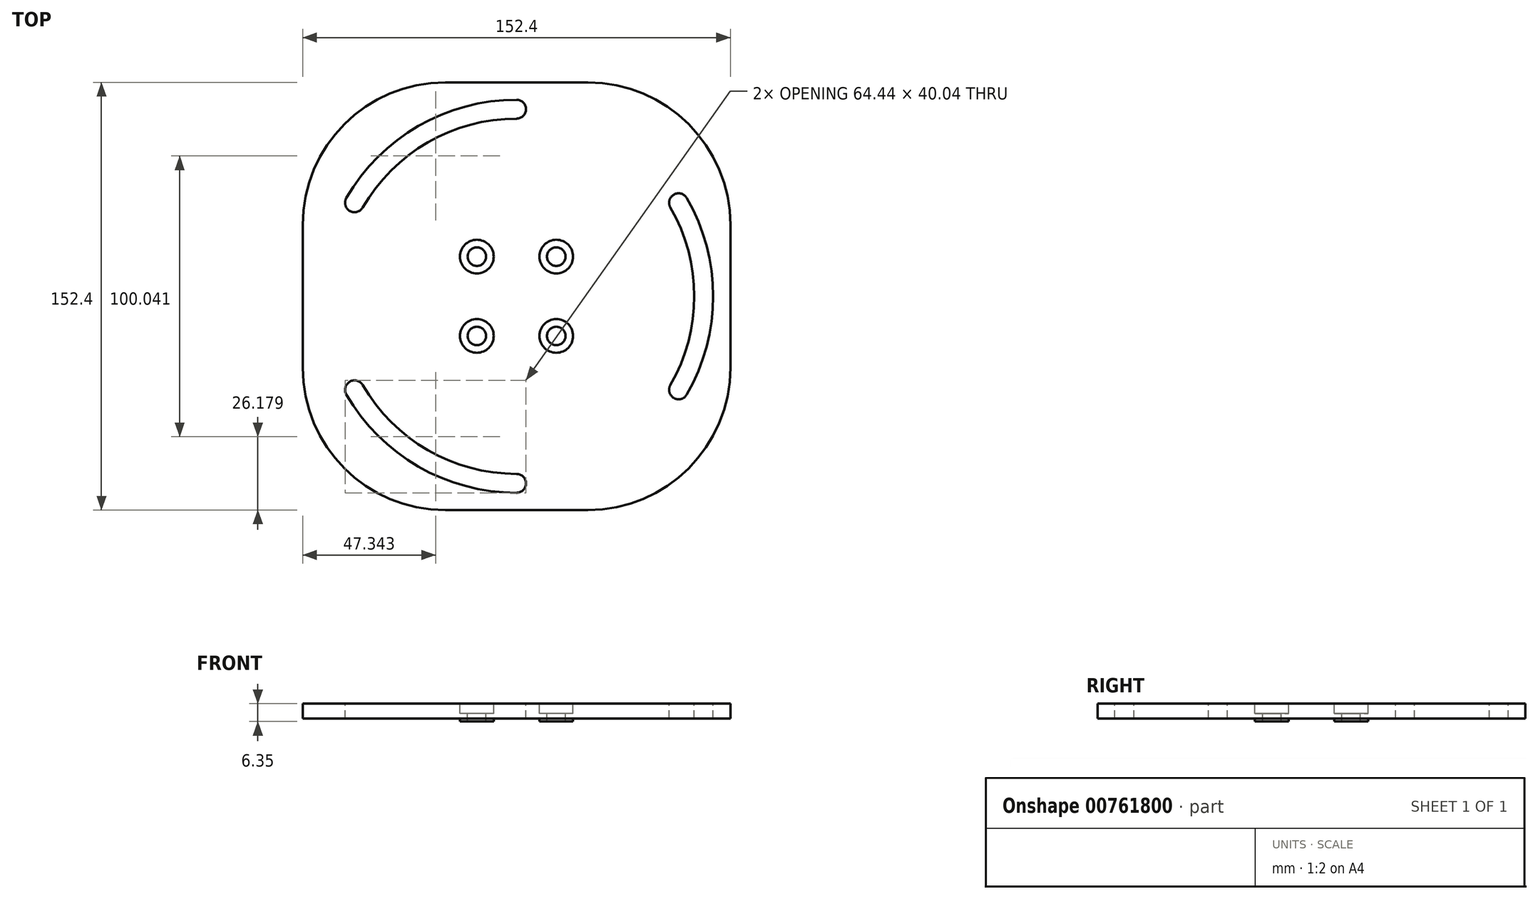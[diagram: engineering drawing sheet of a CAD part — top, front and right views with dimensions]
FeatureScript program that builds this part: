
annotation { "Feature Type Name" : "Feature", "Feature Type Description" : "" }
export const myFeature = defineFeature(function(context is Context, id is Id, definition is map)
    precondition{}
    {
        {
            var Q0;
            Q0=qCreatedBy(makeId("Top.planeOp"),FACE);
            var sketch = newSketch(context, id + "F0", { "sketchPlane" : qUnion([Q0])});
            skLineSegment(sketch, "E0.bottom", {"start": v(-76.2, 76.2) * mm, "end": v(76.2, 76.2) * mm});
            skLineSegment(sketch, "E0.top", {"start": v(-76.2, -76.2) * mm, "end": v(76.2, -76.2) * mm});
            skLineSegment(sketch, "E0.left", {"start": v(-76.2, 76.2) * mm, "end": v(-76.2, -76.2) * mm});
            skLineSegment(sketch, "E0.right", {"start": v(76.2, 76.2) * mm, "end": v(76.2, -76.2) * mm});
            skCircle(sketch, "E1", {"center": v(0, 0) * mm, "radius": 20 * mm, "construction": true});
            skLineSegment(sketch, "E2.bottom", {"start": v(-66.68, 66.68) * mm, "end": v(66.68, 66.68) * mm, "construction": true});
            skLineSegment(sketch, "E2.top", {"start": v(-66.68, -66.68) * mm, "end": v(66.67, -66.68) * mm, "construction": true});
            skLineSegment(sketch, "E2.left", {"start": v(-66.67, 66.68) * mm, "end": v(-66.68, -66.68) * mm, "construction": true});
            skLineSegment(sketch, "E2.right", {"start": v(66.68, 66.68) * mm, "end": v(66.67, -66.68) * mm, "construction": true});
            skLineSegment(sketch, "E3", {"start": v(0, 66.68) * mm, "end": v(0, -66.68) * mm, "construction": true});
            skLineSegment(sketch, "E4", {"start": v(-66.67, 0) * mm, "end": v(66.67, 0) * mm, "construction": true});
            skLineSegment(sketch, "E5.bottom", {"start": v(-14.14, 14.14) * mm, "end": v(14.14, 14.14) * mm});
            skLineSegment(sketch, "E5.top", {"start": v(-14.14, -14.14) * mm, "end": v(14.14, -14.14) * mm});
            skLineSegment(sketch, "E5.left", {"start": v(-14.14, 14.14) * mm, "end": v(-14.14, -14.14) * mm});
            skLineSegment(sketch, "E5.right", {"start": v(14.14, 14.14) * mm, "end": v(14.14, -14.14) * mm});
            skCircle(sketch, "E6", {"center": v(0, 0) * mm, "radius": 66.67 * mm, "construction": true});
            skLineSegment(sketch, "E7", {"start": v(0, 0) * mm, "end": v(-57.74, 33.34) * mm, "construction": true});
            skLineSegment(sketch, "E8", {"start": v(0, 0) * mm, "end": v(-57.74, -33.34) * mm, "construction": true});
            skLineSegment(sketch, "E9", {"start": v(0, 0) * mm, "end": v(57.74, -33.34) * mm, "construction": true});
            skLineSegment(sketch, "E10", {"start": v(0, 0) * mm, "end": v(57.74, 33.34) * mm, "construction": true});
            skArc(sketch, "E11", {"start": v(-60.66, 35.02) * mm, "mid": v(-56.91, 30.08) * mm, "end": v(-55.99, 36.2) * mm});
            skArc(sketch, "E12", {"start": v(0, 63.3) * mm, "mid": v(3.37, 66.68) * mm, "end": v(0, 70.04) * mm});
            skArc(sketch, "E13", {"start": v(60.66, 35.02) * mm, "mid": v(54.5, 34.25) * mm, "end": v(59.35, 30.38) * mm});
            skArc(sketch, "E14", {"start": v(54.83, -31.65) * mm, "mid": v(56.06, -36.25) * mm, "end": v(60.66, -35.02) * mm});
            skArc(sketch, "E15", {"start": v(0, -70.04) * mm, "mid": v(3.37, -66.68) * mm, "end": v(0, -63.3) * mm});
            skArc(sketch, "E16", {"start": v(-54.83, -31.65) * mm, "mid": v(-59.42, -30.42) * mm, "end": v(-60.66, -35.02) * mm});
            skArc(sketch, "E17", {"start": v(-54.83, 31.65) * mm, "mid": v(-31.65, 54.83) * mm, "end": v(0, 63.3) * mm});
            skArc(sketch, "E18", {"start": v(0, 70.04) * mm, "mid": v(-35.02, 60.66) * mm, "end": v(-60.66, 35.02) * mm});
            skArc(sketch, "E19", {"start": v(-54.83, -31.65) * mm, "mid": v(-31.65, -54.83) * mm, "end": v(0, -63.3) * mm});
            skLineSegment(sketch, "E20", {"start": v(0, 0) * mm, "end": v(-60.66, -35.02) * mm, "construction": true});
            skLineSegment(sketch, "E21", {"start": v(0, 0) * mm, "end": v(0, -70.04) * mm, "construction": true});
            skLineSegment(sketch, "E22", {"start": v(0, 0) * mm, "end": v(60.66, -35.02) * mm, "construction": true});
            skLineSegment(sketch, "E23", {"start": v(0, 0) * mm, "end": v(60.66, 35.02) * mm, "construction": true});
            skArc(sketch, "E24", {"start": v(-60.66, -35.02) * mm, "mid": v(-35.02, -60.66) * mm, "end": v(0, -70.04) * mm});
            skArc(sketch, "E25", {"start": v(54.83, -31.65) * mm, "mid": v(63.3, 0) * mm, "end": v(54.83, 31.65) * mm});
            skArc(sketch, "E26", {"start": v(60.66, -35.02) * mm, "mid": v(70.04, 0) * mm, "end": v(60.66, 35.02) * mm});
            skArc(sketch, "E27.trimOffspring", {"start": v(-3.37, 66.68) * mm, "mid": v(-3.37, 66.63) * mm, "end": v(-3.36, 66.6) * mm});
            skArc(sketch, "E28.trimOffspring", {"start": v(-3.36, -66.6) * mm, "mid": v(-3.37, -66.63) * mm, "end": v(-3.37, -66.68) * mm});
            skSolve(sketch);
        }
        {
            var Q0;
            Q0=makeQuery(id+"F0.imprint","IMPRINT",FACE,{"disambiguationData":[TD([[makeQuery(id+"F0.imprint","IMPRINT",EDGE,{"derivedFrom":sQuery(id+"F0.wireOp",EDGE,"E0.bottom")}),-1.0]])]});
            var Q1;
            Q1=makeQuery(id+"F0.imprint","IMPRINT",FACE,{"disambiguationData":[TD([[makeQuery(id+"F0.imprint","IMPRINT",EDGE,{"derivedFrom":sQuery(id+"F0.wireOp",EDGE,"E5.bottom")}),-1.0]])]});
            extrude(context, id + "F1", {"entities" : qUnion([Q0, Q1]), "oppositeDirection" : true, "depth" : 6.35 * mm, "offsetDistance" : 25.4 * mm});
        }
        {
            var Q0;
            Q0=sQuery(id+"F0.wireOp",VERTEX,"E5.right.start");
            var Q1;
            Q1=sQuery(id+"F0.wireOp",VERTEX,"E5.top.end");
            var Q2;
            Q2=sQuery(id+"F0.wireOp",VERTEX,"E5.left.end");
            var Q3;
            Q3=sQuery(id+"F0.wireOp",VERTEX,"E5.bottom.start");
            var Q4;
            Q4=makeQuery(id+"F1.opExtrude","SWEPT_BODY",BODY,{"disambiguationData":[OSD([sQuery(id+"F0.wireOp",EDGE,"E0.bottom"),sQuery(id+"F0.wireOp",EDGE,"E0.top"),sQuery(id+"F0.wireOp",EDGE,"E0.left"),sQuery(id+"F0.wireOp",EDGE,"E0.right"),sQuery(id+"F0.wireOp",EDGE,"XeHkDApb-MA9O-4u2T-mxvz-GZuwpiwDo9aP"),sQuery(id+"F0.wireOp",EDGE,"vUVk7mpQ-ylOQ-OA6W-jopI-vXUm2sK5rRwa"),sQuery(id+"F0.wireOp",EDGE,"vd1RrCug-lLv6-xi6O-alX8-GvBH5Qbzccqz"),sQuery(id+"F0.wireOp",EDGE,"wzc8vz6c-8jZm-Zd6N-sGzb-bpLEjItQo0Bi"),sQuery(id+"F0.wireOp",EDGE,"m4PzrRpF-oZZE-pdqt-a3Ye-l0yXMeVrFHAO"),sQuery(id+"F0.wireOp",EDGE,"lyPhdHaD-ZUAY-RZnG-dhlV-V3pZ9skbXEP6"),sQuery(id+"F0.wireOp",EDGE,"REmQqFtK-cmDS-f0NC-SfeB-U3QxN6EzgIpH"),sQuery(id+"F0.wireOp",EDGE,"HGGWc6S7-uN7V-lp7G-a2WR-cxTkJSfulR2k")])]});
            hole(context, id + "F2", {"style" : HoleStyle.C_BORE, "endStyle" : HoleEndStyle.THROUGH, "holeDiameter" : 6.6 * mm, "cBoreDiameter" : 12 * mm, "cBoreDepth" : 3.5 * mm, "majorDiameter" : 6.35 * mm, "isTappedThrough" : true, "tappedDepth" : 12.7 * mm, "tapClearance" : 3, "locations" : qUnion([Q0, Q1, Q2, Q3]), "scope" : qUnion([Q4])});
        }
        {
            var Q0;
            Q0=makeQuery(id+"F1.opExtrude","SWEPT_EDGE",EDGE,{"disambiguationData":[OSD([sQuery(id+"F0.wireOp",EDGE,"E0.top"),sQuery(id+"F0.wireOp",EDGE,"E0.right")])]});
            var Q1;
            Q1=makeQuery(id+"F1.opExtrude","SWEPT_EDGE",EDGE,{"disambiguationData":[OSD([sQuery(id+"F0.wireOp",EDGE,"E0.top"),sQuery(id+"F0.wireOp",EDGE,"E0.left")])]});
            var Q2;
            Q2=makeQuery(id+"F1.opExtrude","SWEPT_EDGE",EDGE,{"disambiguationData":[OSD([sQuery(id+"F0.wireOp",EDGE,"E0.bottom"),sQuery(id+"F0.wireOp",EDGE,"E0.right")])]});
            var Q3;
            Q3=makeQuery(id+"F1.opExtrude","SWEPT_EDGE",EDGE,{"disambiguationData":[OSD([sQuery(id+"F0.wireOp",EDGE,"E0.bottom"),sQuery(id+"F0.wireOp",EDGE,"E0.left")])]});
            fillet(context, id + "F3", {"entities" : qUnion([Q0, Q1, Q2, Q3]), "radius" : 50.8 * mm, "tangentPropagation" : true, "allowEdgeOverflow" : false});
        }
        {
            var Q0;
            Q0=makeQuery(id+"F1.opExtrude","CAP_FACE",FACE,{"disambiguationData":[OSD([sQuery(id+"F0.wireOp",EDGE,"E0.bottom"),sQuery(id+"F0.wireOp",EDGE,"E0.top"),sQuery(id+"F0.wireOp",EDGE,"E0.left"),sQuery(id+"F0.wireOp",EDGE,"E0.right"),sQuery(id+"F0.wireOp",EDGE,"E11"),sQuery(id+"F0.wireOp",EDGE,"E12"),sQuery(id+"F0.wireOp",EDGE,"E13"),sQuery(id+"F0.wireOp",EDGE,"E14"),sQuery(id+"F0.wireOp",EDGE,"E15"),sQuery(id+"F0.wireOp",EDGE,"E16"),sQuery(id+"F0.wireOp",EDGE,"E17"),sQuery(id+"F0.wireOp",EDGE,"E18"),sQuery(id+"F0.wireOp",EDGE,"E19"),sQuery(id+"F0.wireOp",EDGE,"E24"),sQuery(id+"F0.wireOp",EDGE,"E25"),sQuery(id+"F0.wireOp",EDGE,"E26")])],"isStart":false});
            var sketch = newSketch(context, id + "F4", { "sketchPlane" : qUnion([Q0])});
            skCircle(sketch, "E29", {"center": v(-14.14, 14.14) * mm, "radius": 6 * mm});
            skCircle(sketch, "E30", {"center": v(14.14, -14.14) * mm, "radius": 6 * mm});
            skCircle(sketch, "E31", {"center": v(-14.14, -14.14) * mm, "radius": 6 * mm});
            skCircle(sketch, "E32", {"center": v(14.14, 14.14) * mm, "radius": 6 * mm});
            skSolve(sketch);
        }
        {
            var Q0;
            Q0=makeQuery(id+"F4.imprint","IMPRINT",FACE,{"disambiguationData":[TD([[makeQuery(id+"F4.imprint","IMPRINT",EDGE,{"derivedFrom":sQuery(id+"F4.wireOp",EDGE,"E29")}),-1.0]])]});
            extrude(context, id + "F5", {"entities" : qUnion([Q0]), "operationType" : NewBodyOperationType.REMOVE, "oppositeDirection" : true, "depth" : 1 * mm, "offsetDistance" : 25.4 * mm});
        }
    });
